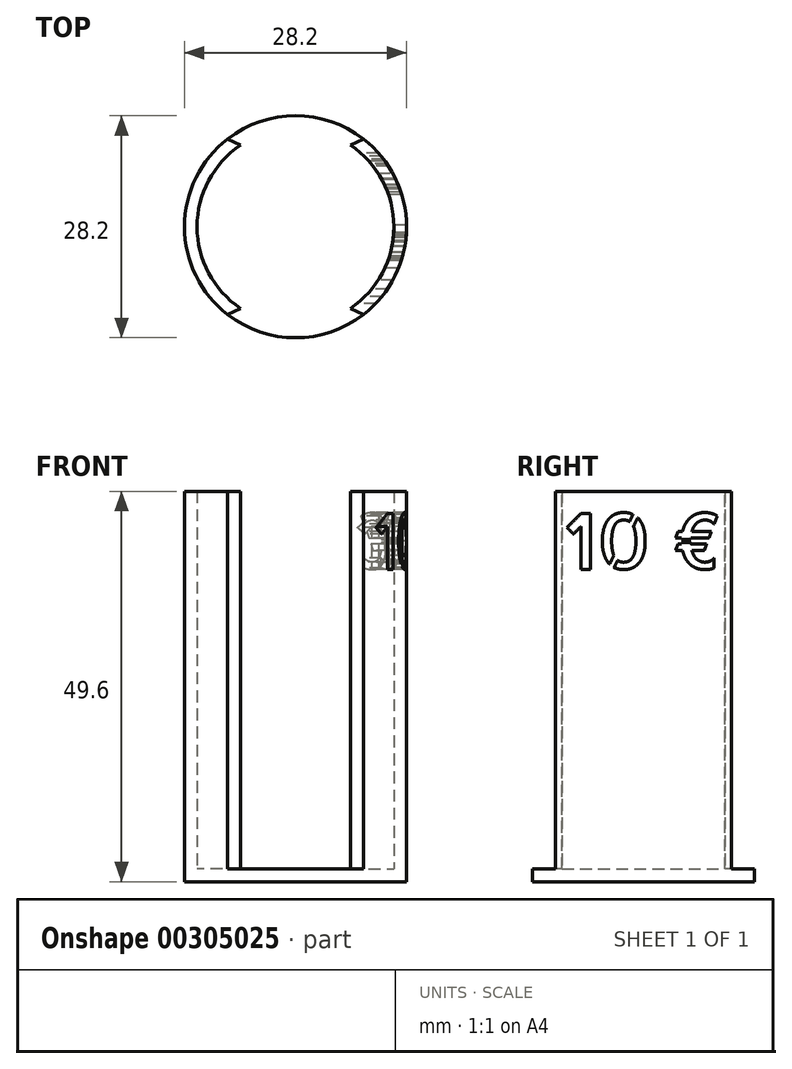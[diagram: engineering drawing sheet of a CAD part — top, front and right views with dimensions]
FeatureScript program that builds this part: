
annotation { "Feature Type Name" : "Feature", "Feature Type Description" : "" }
export const myFeature = defineFeature(function(context is Context, id is Id, definition is map)
    precondition{}
    {
        {
            var Q0;
            Q0=qCreatedBy(makeId("Top.planeOp"),FACE);
            var sketch = newSketch(context, id + "F0", { "sketchPlane" : qUnion([Q0])});
            skCircle(sketch, "E0", {"center": v(0, 0) * mm, "radius": 12.5 * mm});
            skCircle(sketch, "E1.0", {"center": v(0, 0) * mm, "radius": 14.1 * mm});
            skSolve(sketch);
        }
        {
            var Q0;
            Q0=makeQuery(id+"F0.imprint","IMPRINT",FACE,{"disambiguationData":[TD([[makeQuery(id+"F0.imprint","IMPRINT",EDGE,{"derivedFrom":sQuery(id+"F0.wireOp",EDGE,"E0")}),1.0]])]});
            var Q1;
            Q1=makeQuery(id+"F0.imprint","IMPRINT",FACE,{"disambiguationData":[TD([[makeQuery(id+"F0.imprint","IMPRINT",EDGE,{"derivedFrom":sQuery(id+"F0.wireOp",EDGE,"E0")}),-1.0]])]});
            extrude(context, id + "F1", {"entities" : qUnion([Q0, Q1]), "oppositeDirection" : true, "depth" : 1.6 * mm});
        }
        {
            var Q0;
            Q0=makeQuery(id+"F0.imprint","IMPRINT",FACE,{"disambiguationData":[TD([[makeQuery(id+"F0.imprint","IMPRINT",EDGE,{"derivedFrom":sQuery(id+"F0.wireOp",EDGE,"E0")}),-1.0]])]});
            extrude(context, id + "F2", {"entities" : qUnion([Q0]), "operationType" : NewBodyOperationType.ADD, "depth" : 48 * mm});
        }
        {
            var Q0;
            Q0=qCreatedBy(makeId("Front.planeOp"),FACE);
            var sketch = newSketch(context, id + "F3", { "sketchPlane" : qUnion([Q0])});
            skLineSegment(sketch, "E2.bottom", {"start": v(-7, 48) * mm, "end": v(7, 48) * mm});
            skLineSegment(sketch, "E2.top", {"start": v(-7, 0) * mm, "end": v(7, 0) * mm});
            skLineSegment(sketch, "E2.left", {"start": v(-7, 48) * mm, "end": v(-7, 0) * mm});
            skLineSegment(sketch, "E2.right", {"start": v(7, 48) * mm, "end": v(7, 0) * mm});
            skSolve(sketch);
        }
        {
            var Q0;
            Q0=makeQuery(id+"F3.imprint","IMPRINT",FACE,{"disambiguationData":[TD([[makeQuery(id+"F3.imprint","IMPRINT",EDGE,{"derivedFrom":sQuery(id+"F3.wireOp",EDGE,"E2.bottom")}),-1.0]])]});
            extrude(context, id + "F4", {"entities" : qUnion([Q0]), "operationType" : NewBodyOperationType.REMOVE, "endBound" : BoundingType.THROUGH_ALL, "oppositeDirection" : true, "depth" : 25 * mm, "hasSecondDirection" : true, "secondDirectionBound" : SecondDirectionBoundingType.THROUGH_ALL, "secondDirectionOppositeDirection" : false, "secondDirectionDepth" : 25 * mm});
        }
        {
            var Q0;
            {var subQ0=sQuery(id+"F0.wireOp",EDGE,"E1.0");Q0=makeQuery(id+"F4.boolean.opBoolean","INTERSECT",EDGE,{"disambiguationData":[OD(0.0)],"derivedFrom":[makeQuery(id+"F2.boolean.opBoolean","MERGE",FACE,{"derivedFrom":[makeQuery(id+"F1.opExtrude","SWEPT_FACE",FACE,{"disambiguationData":[OSD([subQ0])]}),makeQuery(id+"F2.opExtrude","SWEPT_FACE",FACE,{"disambiguationData":[OSD([subQ0])]})]}),makeQuery(id+"F4.opExtrude","SWEPT_FACE",FACE,{"disambiguationData":[OSD([sQuery(id+"F3.wireOp",EDGE,"E2.left")])]})]});}
            var Q1;
            {var subQ0=sQuery(id+"F0.wireOp",EDGE,"E1.0");Q1=makeQuery(id+"F4.boolean.opBoolean","INTERSECT",EDGE,{"disambiguationData":[OD(0.0)],"derivedFrom":[makeQuery(id+"F2.boolean.opBoolean","MERGE",FACE,{"derivedFrom":[makeQuery(id+"F1.opExtrude","SWEPT_FACE",FACE,{"disambiguationData":[OSD([subQ0])]}),makeQuery(id+"F2.opExtrude","SWEPT_FACE",FACE,{"disambiguationData":[OSD([subQ0])]})]}),makeQuery(id+"F4.opExtrude","SWEPT_FACE",FACE,{"disambiguationData":[OSD([sQuery(id+"F3.wireOp",EDGE,"E2.right")])]})]});}
            var Q2;
            {var subQ0=sQuery(id+"F0.wireOp",EDGE,"E1.0");Q2=makeQuery(id+"F4.boolean.opBoolean","INTERSECT",EDGE,{"disambiguationData":[OD(1.0)],"derivedFrom":[makeQuery(id+"F2.boolean.opBoolean","MERGE",FACE,{"derivedFrom":[makeQuery(id+"F1.opExtrude","SWEPT_FACE",FACE,{"disambiguationData":[OSD([subQ0])]}),makeQuery(id+"F2.opExtrude","SWEPT_FACE",FACE,{"disambiguationData":[OSD([subQ0])]})]}),makeQuery(id+"F4.opExtrude","SWEPT_FACE",FACE,{"disambiguationData":[OSD([sQuery(id+"F3.wireOp",EDGE,"E2.left")])]})]});}
            var Q3;
            {var subQ0=sQuery(id+"F0.wireOp",EDGE,"E1.0");Q3=makeQuery(id+"F4.boolean.opBoolean","INTERSECT",EDGE,{"disambiguationData":[OD(1.0)],"derivedFrom":[makeQuery(id+"F2.boolean.opBoolean","MERGE",FACE,{"derivedFrom":[makeQuery(id+"F1.opExtrude","SWEPT_FACE",FACE,{"disambiguationData":[OSD([subQ0])]}),makeQuery(id+"F2.opExtrude","SWEPT_FACE",FACE,{"disambiguationData":[OSD([subQ0])]})]}),makeQuery(id+"F4.opExtrude","SWEPT_FACE",FACE,{"disambiguationData":[OSD([sQuery(id+"F3.wireOp",EDGE,"E2.right")])]})]});}
            chamfer(context, id + "F5", {"entities" : qUnion([Q0, Q1, Q2, Q3]), "width" : 1 * mm, "tangentPropagation" : true});
        }
        {
            var Q0;
            Q0=qCreatedBy(makeId("Right.planeOp"),FACE);
            var sketch = newSketch(context, id + "F6", { "sketchPlane" : qUnion([Q0])});
            skText(sketch, "E3", { "text": "10 €", "fontName": "AllertaStencil-Regular.ttf"});
            const initialGuessF6  = {"E3": [-0.01, 0.03809, 1, 0, 0.0071]};
            skSetInitialGuess(sketch, initialGuessF6);
            skSolve(sketch);
        }
        {
            var Q0;
            Q0 = qSketchRegion(id + "F6", true);
            extrude(context, id + "F7", {"entities" : qUnion([Q0]), "operationType" : NewBodyOperationType.REMOVE, "depth" : 25 * mm});
        }
    });
